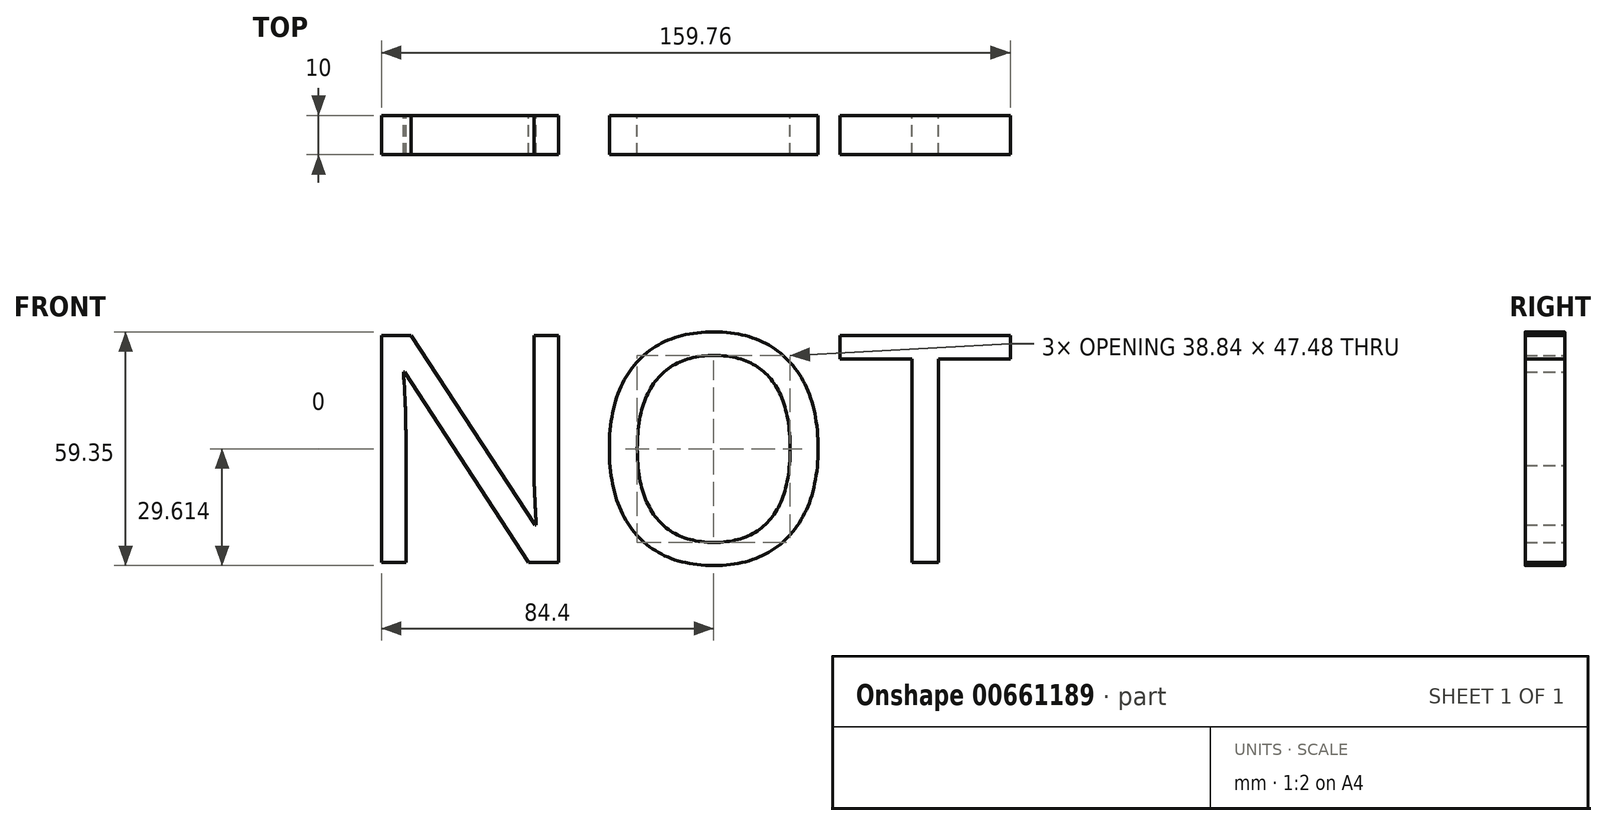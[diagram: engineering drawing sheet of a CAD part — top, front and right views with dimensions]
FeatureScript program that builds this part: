
annotation { "Feature Type Name" : "Feature", "Feature Type Description" : "" }
export const myFeature = defineFeature(function(context is Context, id is Id, definition is map)
    precondition{}
    {
        {
            var Q0;
            Q0=qCreatedBy(makeId("Front.planeOp"),FACE);
            var sketch = newSketch(context, id + "F0", { "sketchPlane" : qUnion([Q0])});
            skText(sketch, "E0", { "text": "NOT", "fontName": "OpenSans-Regular.ttf"});
            const initialGuessF0  = {"E0": [-0.0439, -0.02605, 1, 0, 0.05814]};
            skSetInitialGuess(sketch, initialGuessF0);
            skSolve(sketch);
        }
        {
            var Q0;
            Q0 = qSketchRegion(id + "F0", true);
            extrude(context, id + "F1", {"entities" : qUnion([Q0]), "depth" : 10 * mm, "offsetDistance" : 25.4 * mm});
        }
    });
